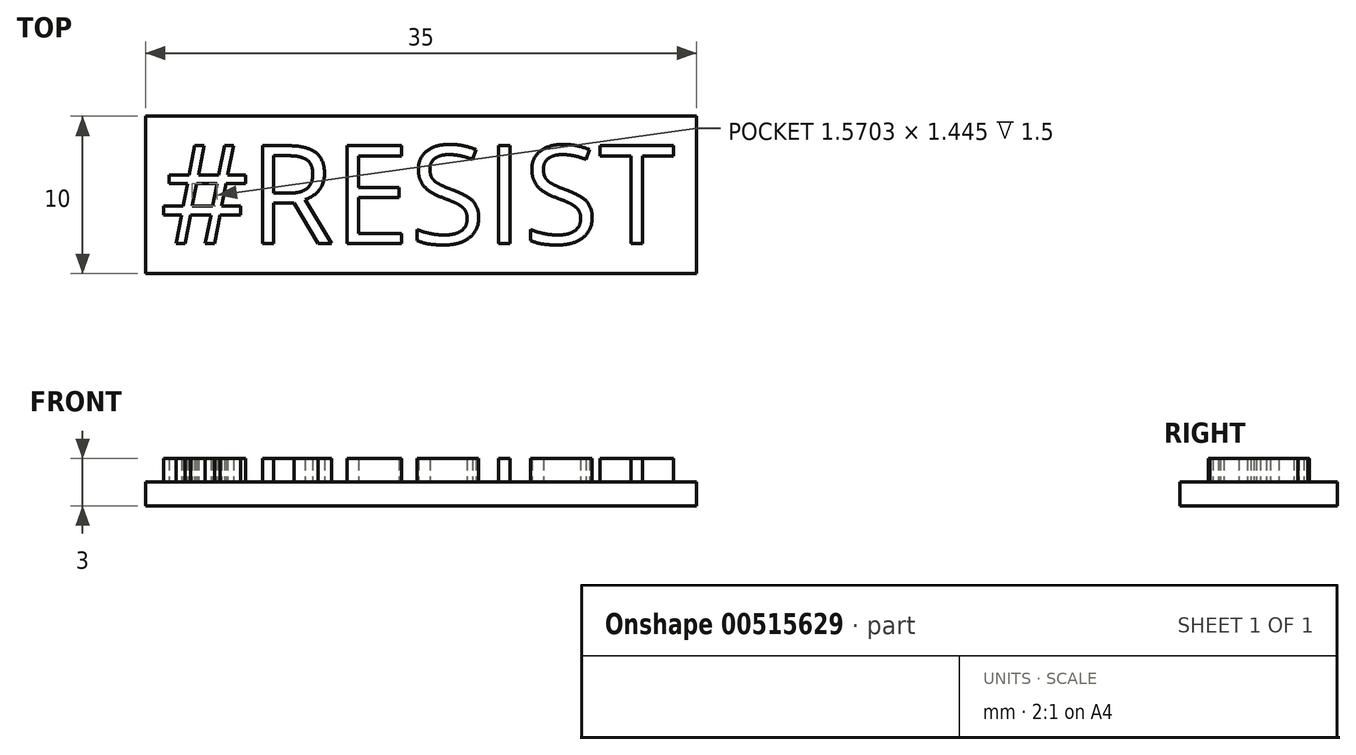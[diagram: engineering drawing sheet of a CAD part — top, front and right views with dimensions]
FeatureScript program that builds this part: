
annotation { "Feature Type Name" : "Feature", "Feature Type Description" : "" }
export const myFeature = defineFeature(function(context is Context, id is Id, definition is map)
    precondition{}
    {
        {
            var Q0;
            Q0=qCreatedBy(makeId("Top.planeOp"),FACE);
            var sketch = newSketch(context, id + "F0", { "sketchPlane" : qUnion([Q0])});
            skLineSegment(sketch, "E0.bottom", {"start": v(17.5, -5) * mm, "end": v(-17.5, -5) * mm});
            skLineSegment(sketch, "E0.top", {"start": v(17.5, 5) * mm, "end": v(-17.5, 5) * mm});
            skLineSegment(sketch, "E0.left", {"start": v(17.5, -5) * mm, "end": v(17.5, 5) * mm});
            skLineSegment(sketch, "E0.right", {"start": v(-17.5, -5) * mm, "end": v(-17.5, 5) * mm});
            skPoint(sketch, "E0.middle", {"position": v(0, 0) * mm});
            skSolve(sketch);
        }
        {
            var Q0;
            Q0=makeQuery(id+"F0.imprint","IMPRINT",FACE,{"disambiguationData":[TD([[makeQuery(id+"F0.imprint","IMPRINT",EDGE,{"derivedFrom":sQuery(id+"F0.wireOp",EDGE,"E0.bottom")}),-1.0]])]});
            extrude(context, id + "F1", {"entities" : qUnion([Q0]), "depth" : 1.5 * mm, "offsetDistance" : 25 * mm});
        }
        {
            var Q0;
            Q0=qCreatedBy(makeId("Top.planeOp"),FACE);
            var sketch = newSketch(context, id + "F2", { "sketchPlane" : qUnion([Q0])});
            skText(sketch, "E1", { "text": "#RESIST", "fontName": "OpenSans-Regular.ttf"});
            const initialGuessF2  = {"E1": [-0.01656, -0.0031, 1, 0, 0.00627]};
            skSetInitialGuess(sketch, initialGuessF2);
            skSolve(sketch);
        }
        {
            var Q0;
            Q0 = qSketchRegion(id + "F2", true);
            extrude(context, id + "F3", {"entities" : qUnion([Q0]), "operationType" : NewBodyOperationType.ADD, "depth" : 3 * mm, "offsetDistance" : 25 * mm});
        }
    });
